# Revit family: Lighting_Fixture-Wall-Astro-Osaka
name_source: partatom
category: Lighting Fixtures
revit_build: Autodesk Revit 2014 (Build: 20130308_1515(x64)
units: mm (PartAtom-declared; Revit-internal decimal feet)

## types (3) — shared parameters
Apparent Load = 30 VA
Assembly Code = D5020200
Class = 2
Color Filter = 16777215
Description = Wall Light
Dimmable = No
Dimming Lamp Color Temperature Shift = <None>
Emit Shape Visible in Rendering = No
Emit from Circle Diameter = 276.16 mm  [stored 0.906037 ft]
Energy Efficiency Rating = A
Height = 310 mm  [stored 1.01706 ft]
IP Rating = IP44
Lamp = 4 pin 2D
Lamp included = Yes
Length = 95 mm
Light Source From Wall = 60 mm  [stored 0.19685 ft]
Luminaire Lamp Efficiency Rating = A-B
Manufacturer = Astro Lighting Ltd, CM20 2DP
Mountable on normally flammable surfaces = Yes
Number of Poles = 1
Photometric Web File = 0387 OSAKA.ies
Product Documentation = http://www.astrolighting.co.uk
Suitable for bathroom zone = Zones 2 and 3
Tilt Angle = 90.00°
Type Comments = Can be mounted on ceiling or wall. Includes integral electronic ballast.
URL = www.astrolighting.co.uk
Voltage = 230 V
Wattage Comments = 28w
Weight = 1.3kg
Width = 310 mm  [stored 1.01706 ft]

## per-type parameters (varying)
| type | Casing Material | Model |
| 0387 Osaka (Chrome) | Astro - Steel - Chrome Finish | 0387 Osaka Chrome |
| 0906 Osaka (Matt Nickel) | Astro - Steel - Matt Nickel | 0906 Osaka Matt Nickel |
| 7383 Osaka (White) | Astro - Steel - White | 7383 Osaka (White) |

note: [stored X ft] marks values corroborated as IEEE doubles in the binary element streams (Revit-internal decimal feet)

## geometry (parser evidence)
native form markers: Sweep x2
no freeform markers — native parametric forms only
